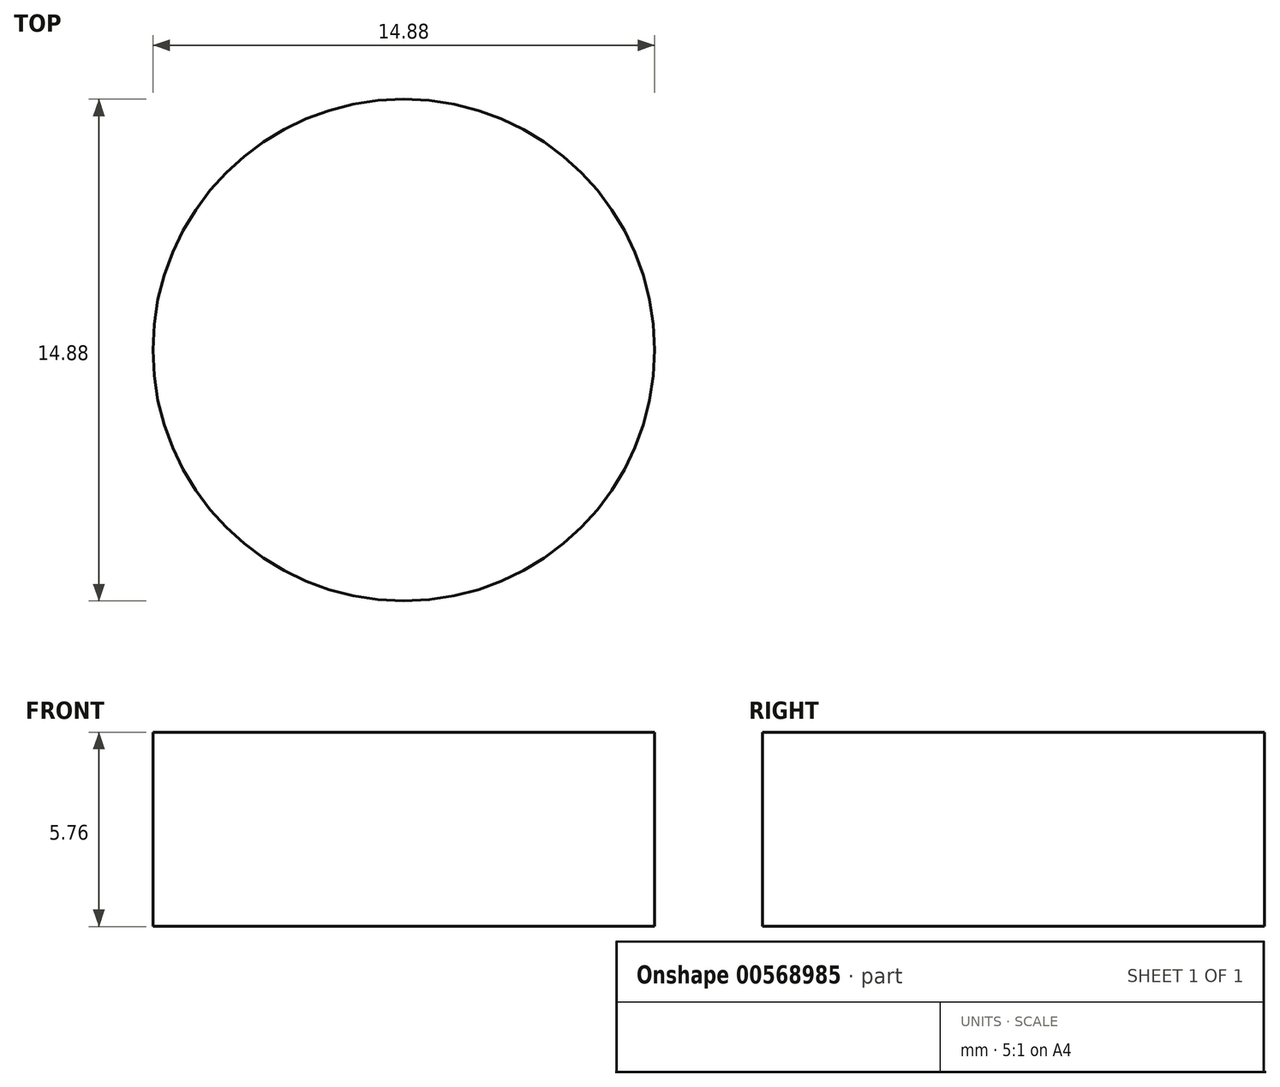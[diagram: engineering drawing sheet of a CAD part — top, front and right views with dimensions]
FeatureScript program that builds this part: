
annotation { "Feature Type Name" : "Feature", "Feature Type Description" : "" }
export const myFeature = defineFeature(function(context is Context, id is Id, definition is map)
    precondition{}
    {
        {
            var Q0;
            Q0=qCreatedBy(makeId("Front.planeOp"),FACE);
            var sketch = newSketch(context, id + "F0", { "sketchPlane" : qUnion([Q0])});
            skLineSegment(sketch, "E0.bottom", {"start": v(-7.44, 4.7) * mm, "end": v(7.44, 4.7) * mm});
            skLineSegment(sketch, "E0.top", {"start": v(-7.44, -1.05) * mm, "end": v(7.44, -1.05) * mm});
            skLineSegment(sketch, "E0.left", {"start": v(-7.44, 4.7) * mm, "end": v(-7.44, -1.05) * mm});
            skLineSegment(sketch, "E0.right", {"start": v(7.44, 4.7) * mm, "end": v(7.44, -1.05) * mm});
            skLineSegment(sketch, "E1", {"start": v(0, 4.7) * mm, "end": v(0, -1.05) * mm});
            skSolve(sketch);
        }
        {
            var Q0;
            {var subQ0=sQuery(id+"F0.wireOp",EDGE,"E0.left");Q0=makeQuery(id+"F0.imprint","IMPRINT",FACE,{"disambiguationData":[TD([[makeQuery(id+"F0.imprint","IMPRINT",EDGE,{"derivedFrom":subQ0}),1.0]])]});}
            var Q1;
            Q1=sQuery(id+"F0.wireOp",EDGE,"E1");
            revolve(context, id + "F1", {"entities" : qUnion([Q0]), "axis" : qUnion([Q1]), "revolveType" : RevolveType.FULL});
        }
    });
